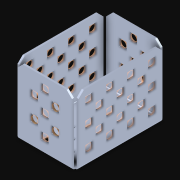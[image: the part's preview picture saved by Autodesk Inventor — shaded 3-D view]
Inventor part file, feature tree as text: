
AUTODESK INVENTOR PART (.ipt)
format: ipt  version: 2021 (Build 250183000, 183)  size: 738,816 bytes
history: native  units: in
note: dims shown in document units (in); Inventor stores cm internally (conversion verified against a paired STEP export)
features: other x62, extrude x61, pattern_linear x10, sketch x5, imported_body x1
ambient origin geometry x8: Origin, YZ Plane, XZ Plane, XY Plane, X Axis, Y Axis, Z Axis, Center Point
bodies: Body1 (feature_tree), Body2 (feature_tree), Body3 (feature_tree), Body4 (feature_tree), Body5 (feature_tree), Body6 (feature_tree), Body7 (feature_tree), Body8 (feature_tree), Body9 (feature_tree), Body10 (feature_tree), Body11 (feature_tree), Body12 (feature_tree), Body13 (feature_tree), Body14 (feature_tree), Body15 (feature_tree), Body16 (feature_tree), Body17 (feature_tree), Body18 (feature_tree), Body19 (feature_tree), Body20 (feature_tree), Body21 (feature_tree), Body22 (feature_tree), Body23 (feature_tree), Body24 (feature_tree), Body25 (feature_tree), Body26 (feature_tree), Body27 (feature_tree), Body28 (feature_tree), Body29 (feature_tree), Body30 (feature_tree), Body31 (feature_tree), Body32 (feature_tree), Body33 (feature_tree), Body34 (feature_tree), Body35 (feature_tree), Body36 (feature_tree), Body37 (feature_tree), Body38 (feature_tree), Body39 (feature_tree), Body40 (feature_tree), Body41 (feature_tree), Body42 (feature_tree), Body43 (feature_tree), Body44 (feature_tree), Body45 (feature_tree), Body46 (feature_tree), Body47 (feature_tree), Body48 (feature_tree), Body49 (feature_tree), Body50 (feature_tree), Body51 (feature_tree), Body52 (feature_tree), Body53 (feature_tree), Body54 (feature_tree), Body55 (feature_tree), Body56 (feature_tree), Body57 (feature_tree), Body58 (feature_tree), Body59 (feature_tree), Body60 (feature_tree), Body61 (feature_tree), Body62 (feature_tree)
feature tree (139):
  parser-record x1  (decoder bookkeeping rows leaked as tree rows — omitted from the tree; the rows remain in map.json)
  imported_body  "Base1"
  pattern_linear  "Rectangular Pattern1"  Count1=3 Spacing1=0.5in
  pattern_linear  "Rectangular Pattern2"  Count1=2 Spacing1=0.5in
  pattern_linear  "Rectangular Pattern3"  Count1=2 Spacing1=0.5in
  pattern_linear  "Rectangular Pattern4"  Count1=4 Spacing1=0.5in
  pattern_linear  "Rectangular Pattern5"  Count1=3 Spacing1=0.5in
  pattern_linear  "Rectangular Pattern6"  Count1=3 Spacing1=0.5in
  pattern_linear  "Rectangular Pattern7"  Count1=2 Spacing1=0.5in
  pattern_linear  "Rectangular Pattern8"  Count1=4 Spacing1=0.5in
  pattern_linear  "Rectangular Pattern9"  Count1=3 Spacing1=0.5in
  pattern_linear  "Rectangular Pattern10"  Spacing1=0.046in  [1 undecoded]
  other  "Srf1"
  other  "Srf2"
  other  "Srf3"
  other  "Srf4"
  other  "Srf5"
  other  "Srf6"
  other  "Srf7"
  other  "Srf8"
  other  "Srf9"
  other  "Srf10"
  other  "Srf11"
  other  "Srf12"
  other  "Srf13"
  other  "Srf14"
  other  "Srf15"
  other  "Srf16"
  other  "Srf17"
  other  "Srf18"
  other  "Srf19"
  other  "Srf20"
  other  "Srf21"
  other  "Srf22"
  other  "Srf23"
  other  "Srf24"
  other  "Srf25"
  other  "Srf26"
  other  "Srf27"
  other  "Srf28"
  other  "Srf29"
  other  "Srf30"
  other  "Srf31"
  other  "Srf32"
  other  "Srf33"
  other  "Srf34"
  other  "Srf35"
  other  "Srf36"
  other  "Srf37"
  sketch  "Sketch6"  dims[d70=0.046in d71=0.0in d72=1.1811in d74=0.5in]
  other  "Srf38"
  other  "Srf39"
  other  "Srf40"
  other  "Srf41"
  other  "Srf42"
  other  "Srf43"
  sketch  "Sketch7"  dims[d76=0.046in d77=0.0in d78=0.7874in d80=0.5in d81=0.7874in d83=0.5in]
  other  "Srf44"
  other  "Srf45"
  other  "Srf46"
  sketch  "Sketch8"  dims[d85=0.046in d86=0.0in d87=1.5748in d89=0.5in d90=1.1811in d92=0.5in]
  other  "Srf47"
  other  "Srf48"
  other  "Srf49"
  other  "Srf50"
  sketch  "Sketch9"  dims[d94=0.046in d95=0.0in d96=1.1811in d98=0.5in d99=0.7874in d101=0.5in]
  other  "Srf51"
  other  "Srf52"
  other  "Srf53"
  other  "Srf54"
  other  "Srf55"
  other  "Srf56"
  other  "Srf57"
  other  "Srf58"
  sketch  "Sketch10"  dims[d103=0.046in d104=0.0in d105=1.5748in d107=0.5in d108=1.1811in d110=0.5in d112=0.046in d113=0.0in d114=1.1811in d116=0.5in d117=0.7874in d119=0.5in d121=0.046in d122=0.0in d123=1.1811in d125=0.5in d127=0.046in d128=0.0in d129=0.7874in d131=0.5in d132=0.7874in d134=0.5in d136=0.046in d137=0.0in d138=1.5748in d140=0.5in d141=0.7874in d143=0.5in d145=0.046in d146=0.0in d147=1.1811in d149=0.5in]
  other  "Srf59"
  other  "Srf60"
  other  "Srf61"
  extrude  "ExtrusionSrf1"  Depth=0.5in
  extrude  "ExtrusionSrf4"  Depth=0.5in
  extrude  "ExtrusionSrf8"  Depth=0.046in TaperAngle=0.0deg
  extrude  "ExtrusionSrf20"  Depth=0.5in
  extrude  "ExtrusionSrf26"  Depth=0.046in TaperAngle=0.0deg
  extrude  "ExtrusionSrf38"  Depth=0.5in
  extrude  "ExtrusionSrf44"  Depth=0.5in
  extrude  "ExtrusionSrf47"  Depth=0.046in TaperAngle=0.0deg
  extrude  "ExtrusionSrf51"  Depth=0.5in
  extrude  "ExtrusionSrf59"  Depth=0.5in
  extrude  "ExtrusionSrf2"  Depth=0.046in TaperAngle=0.0deg
  extrude  "ExtrusionSrf3"  Depth=0.5in
  extrude  "ExtrusionSrf5"  [1 undecoded]
  extrude  "ExtrusionSrf6"  [1 undecoded]
  extrude  "ExtrusionSrf7"  [1 undecoded]
  extrude  "ExtrusionSrf9"  [1 undecoded]
  extrude  "ExtrusionSrf10"  [1 undecoded]
  extrude  "ExtrusionSrf11"  [1 undecoded]
  extrude  "ExtrusionSrf12"  [1 undecoded]
  extrude  "ExtrusionSrf13"  [1 undecoded]
  extrude  "ExtrusionSrf14"  [1 undecoded]
  extrude  "ExtrusionSrf15"  [1 undecoded]
  extrude  "ExtrusionSrf16"  [1 undecoded]
  extrude  "ExtrusionSrf17"  [1 undecoded]
  extrude  "ExtrusionSrf18"  [1 undecoded]
  extrude  "ExtrusionSrf19"  [1 undecoded]
  extrude  "ExtrusionSrf21"  [1 undecoded]
  extrude  "ExtrusionSrf22"  [1 undecoded]
  extrude  "ExtrusionSrf23"  [1 undecoded]
  extrude  "ExtrusionSrf24"  [1 undecoded]
  extrude  "ExtrusionSrf25"  [1 undecoded]
  extrude  "ExtrusionSrf27"  [1 undecoded]
  extrude  "ExtrusionSrf28"  [1 undecoded]
  extrude  "ExtrusionSrf29"  [1 undecoded]
  extrude  "ExtrusionSrf30"  [1 undecoded]
  extrude  "ExtrusionSrf31"  [1 undecoded]
  extrude  "ExtrusionSrf32"  [1 undecoded]
  extrude  "ExtrusionSrf33"  [1 undecoded]
  extrude  "ExtrusionSrf34"  [1 undecoded]
  extrude  "ExtrusionSrf35"  [1 undecoded]
  extrude  "ExtrusionSrf36"  [1 undecoded]
  extrude  "ExtrusionSrf37"  [1 undecoded]
  extrude  "ExtrusionSrf39"  [1 undecoded]
  extrude  "ExtrusionSrf40"  [1 undecoded]
  extrude  "ExtrusionSrf41"  [1 undecoded]
  extrude  "ExtrusionSrf42"  [1 undecoded]
  extrude  "ExtrusionSrf43"  [1 undecoded]
  extrude  "ExtrusionSrf45"  [1 undecoded]
  extrude  "ExtrusionSrf46"  [1 undecoded]
  extrude  "ExtrusionSrf48"  [1 undecoded]
  extrude  "ExtrusionSrf49"  [1 undecoded]
  extrude  "ExtrusionSrf50"  [1 undecoded]
  extrude  "ExtrusionSrf52"  [1 undecoded]
  extrude  "ExtrusionSrf53"  [1 undecoded]
  extrude  "ExtrusionSrf54"  [1 undecoded]
  extrude  "ExtrusionSrf55"  [1 undecoded]
  extrude  "ExtrusionSrf56"  [1 undecoded]
  extrude  "ExtrusionSrf57"  [1 undecoded]
  extrude  "ExtrusionSrf58"  [1 undecoded]
  extrude  "ExtrusionSrf60"  [1 undecoded]
  extrude  "ExtrusionSrf61"  [1 undecoded]
note: 50 required parameter values undecoded (feature->parameter linkage not recoverable at this tier; creation-order binding heuristic only, values carry confidence <= 0.55)
